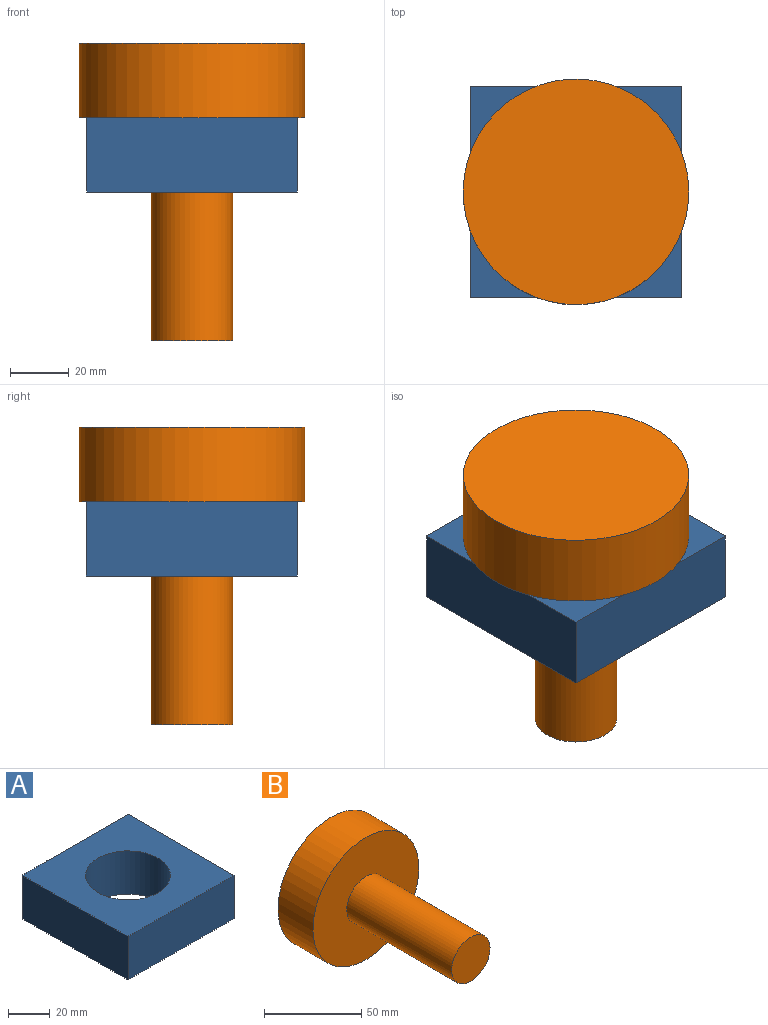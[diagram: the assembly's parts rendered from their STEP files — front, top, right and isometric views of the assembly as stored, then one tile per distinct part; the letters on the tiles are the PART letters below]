
ASSEMBLY  parts=2 mates=1
PART A: 7 faces, bbox 71.9x71.9x25.4 mm
  f0: plane 71.89x25.4mm, normal (-1,0,0), area 1826.1mm2, adj f1,f4,f5,f6
  f1: plane 71.89x25.4mm, normal (0,-1,0), area 1826.1mm2, adj f0,f2,f5,f6
  f2: plane 71.89x25.4mm, normal (1,0,0), area 1826.1mm2, adj f1,f4,f5,f6
  f3: cylinder r=20.32mm len=40.64mm, axis (0,0,-1), area 3243.2mm2, adj f5,f6
  f4: plane 71.89x25.4mm, normal (0,1,0), area 1826.1mm2, adj f0,f2,f5,f6
  f5: plane 71.89x71.89mm, normal (0,0,1), area 3871.4mm2, adj f0,f1,f2,f3,f4
  f6: plane 71.89x71.89mm, normal (0,0,-1), area 3871.4mm2, adj f0,f1,f2,f3,f4
PART B: 5 faces, bbox 76.9x101.6x76.9 mm
  f0: cylinder r=13.92mm len=76.2mm, axis (0,1,0), area 6663.1mm2, adj f1,f4
  f1: plane 27.83x27.83mm, normal (0,-1,0), area 608.5mm2, adj f0
  f2: cylinder r=38.46mm len=76.93mm, axis (0,-1,0), area 6138.5mm2, adj f3,f4
  f3: plane 76.93x76.93mm, normal (0,1,0), area 4647.8mm2, adj f2
  f4: plane 76.93x76.93mm, normal (0,-1,0), area 4039.3mm2, adj f0,f2
PLACE A t=(-4.66,-8.52,1.35)mm fixed
PLACE B rot(axis=(0.2,-0.69,-0.69),157.5deg) t=(31.29,27.43,26.75)mm
MATE revolute A.f3 <-> B.f0  axis (0,0,-1) through (31.29,27.43,26.75)mm
